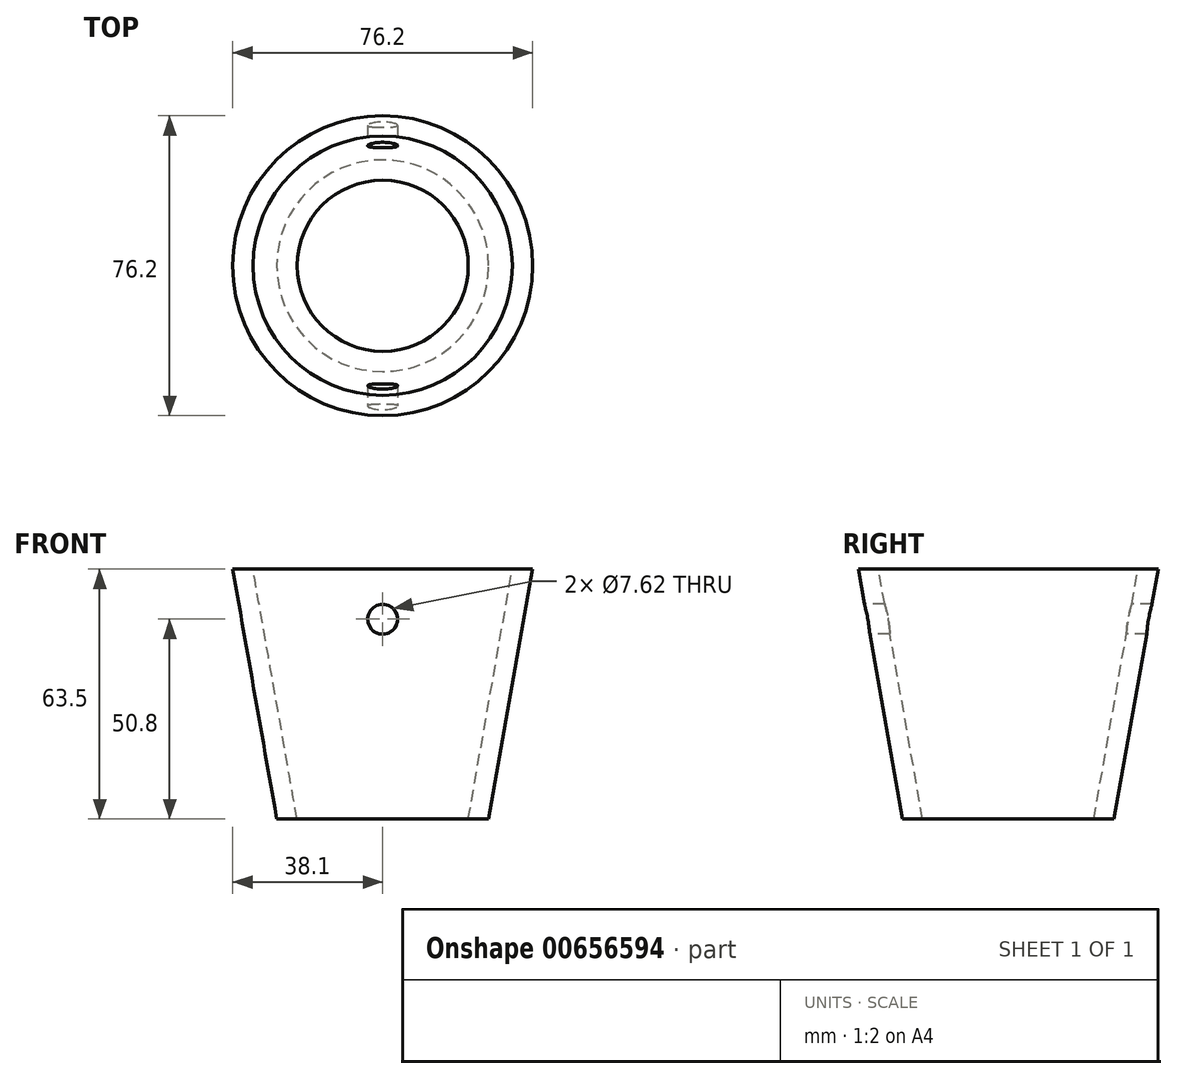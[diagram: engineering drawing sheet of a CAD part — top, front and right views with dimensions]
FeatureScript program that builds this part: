
annotation { "Feature Type Name" : "Feature", "Feature Type Description" : "" }
export const myFeature = defineFeature(function(context is Context, id is Id, definition is map)
    precondition{}
    {
        {
            var Q0;
            Q0=qCreatedBy(makeId("Front.planeOp"),FACE);
            var sketch = newSketch(context, id + "F0", { "sketchPlane" : qUnion([Q0])});
            skLineSegment(sketch, "E0", {"start": v(0, 63.5) * mm, "end": v(-38.1, 63.5) * mm});
            skLineSegment(sketch, "E1", {"start": v(-38.1, 63.5) * mm, "end": v(-26.9, 0) * mm});
            skLineSegment(sketch, "E2", {"start": v(-26.9, 0) * mm, "end": v(0, 0) * mm});
            skLineSegment(sketch, "E3", {"start": v(0, 0) * mm, "end": v(0, 63.5) * mm});
            skLineSegment(sketch, "E4", {"start": v(-32.94, 63.5) * mm, "end": v(-21.74, 0) * mm});
            skCircle(sketch, "E5", {"center": v(0, 50.8) * mm, "radius": 3.81 * mm});
            skSolve(sketch);
        }
        {
            var Q0;
            Q0=makeQuery(id+"F0.imprint","IMPRINT",FACE,{"disambiguationData":[TD([[makeQuery(id+"F0.imprint","IMPRINT",EDGE,{"derivedFrom":sQuery(id+"F0.wireOp",EDGE,"E0")}),1.0]])]});
            var Q1;
            Q1=sQuery(id+"F0.wireOp",EDGE,"E3");
            revolve(context, id + "F1", {"entities" : qUnion([Q0]), "axis" : qUnion([Q1]), "revolveType" : RevolveType.FULL});
        }
        {
            var Q0;
            {var subQ0=sQuery(id+"F0.wireOp",EDGE,"E3");Q0=makeQuery(id+"F0.imprint","IMPRINT",FACE,{"disambiguationData":[TD([[makeQuery(id+"F0.imprint","IMPRINT",EDGE,{"derivedFrom":subQ0}),1.0]])]});}
            var Q1;
            Q1=sQuery(id+"F0.wireOp",EDGE,"E3");
            revolve(context, id + "F2", {"operationType" : NewBodyOperationType.REMOVE, "entities" : qUnion([Q0]), "axis" : qUnion([Q1]), "revolveType" : RevolveType.FULL, "oppositeDirection" : true});
        }
        {
            var Q0;
            {var subQ0=sQuery(id+"F0.wireOp",EDGE,"E5");var subQ1=sQuery(id+"F0.wireOp",EDGE,"E3");var subQ2=makeQuery(id+"F0.imprint","INTERSECT",VERTEX,{"disambiguationData":[OD(0.0)],"derivedFrom":[subQ1,subQ0]});Q0=makeQuery(id+"F0.imprint","IMPRINT",FACE,{"disambiguationData":[TD([[makeQuery(id+"F0.imprint","IMPRINT",EDGE,{"disambiguationData":[TD([[subQ2,-1.0]])],"derivedFrom":subQ1}),1.0]])]});}
            var Q1;
            {var subQ0=sQuery(id+"F0.wireOp",EDGE,"E5");var subQ1=sQuery(id+"F0.wireOp",EDGE,"E3");var subQ2=makeQuery(id+"F0.imprint","INTERSECT",VERTEX,{"disambiguationData":[OD(0.0)],"derivedFrom":[subQ1,subQ0]});Q1=makeQuery(id+"F0.imprint","IMPRINT",FACE,{"disambiguationData":[TD([[makeQuery(id+"F0.imprint","IMPRINT",EDGE,{"disambiguationData":[TD([[subQ2,-1.0]])],"derivedFrom":subQ1}),-1.0]])]});}
            extrude(context, id + "F3", {"entities" : qUnion([Q0, Q1]), "operationType" : NewBodyOperationType.REMOVE, "oppositeDirection" : true, "depth" : 157.48 * mm, "offsetDistance" : 25.4 * mm, "symmetric" : true});
        }
    });
